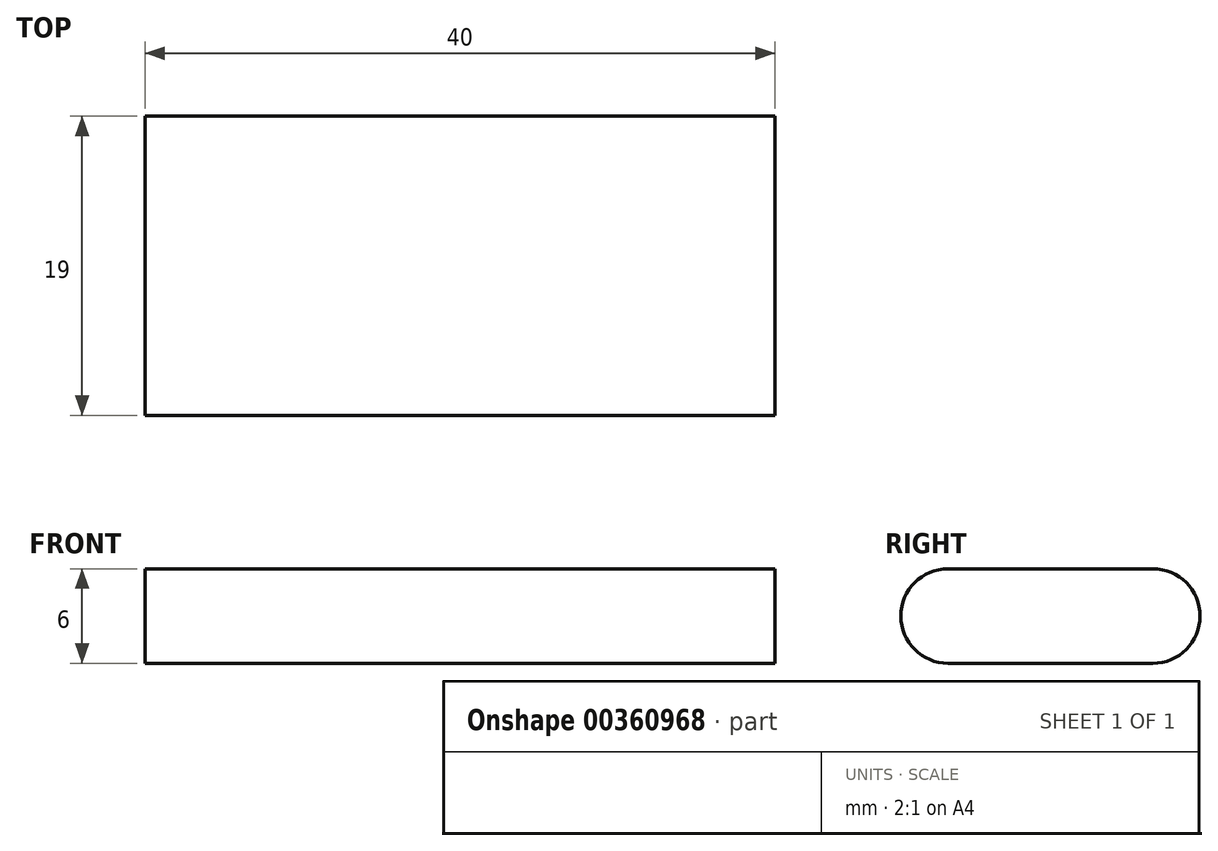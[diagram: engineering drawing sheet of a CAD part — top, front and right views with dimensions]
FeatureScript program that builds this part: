
annotation { "Feature Type Name" : "Feature", "Feature Type Description" : "" }
export const myFeature = defineFeature(function(context is Context, id is Id, definition is map)
    precondition{}
    {
        {
            var Q0;
            Q0=qCreatedBy(makeId("Right.planeOp"),FACE);
            var sketch = newSketch(context, id + "F0", { "sketchPlane" : qUnion([Q0])});
            skLineSegment(sketch, "E0.bottom", {"start": v(6.5, 3) * mm, "end": v(-6.5, 3) * mm});
            skLineSegment(sketch, "E0.top", {"start": v(6.5, -3) * mm, "end": v(-6.5, -3) * mm});
            skLineSegment(sketch, "E0.left", {"start": v(9.5, 0) * mm, "end": v(9.5, 0) * mm});
            skLineSegment(sketch, "E0.right", {"start": v(-9.5, 0) * mm, "end": v(-9.5, 0) * mm});
            skPoint(sketch, "E0.middle", {"position": v(0, 0) * mm});
            skPoint(sketch, "E1.visualSharp", {"position": v(-9.5, 3) * mm});
            skArc(sketch, "E1.filletArc", {"start": v(-6.5, 3) * mm, "mid": v(-8.62, 2.12) * mm, "end": v(-9.5, 0) * mm});
            skPoint(sketch, "E2.visualSharp", {"position": v(-9.5, -3) * mm});
            skArc(sketch, "E2.filletArc", {"start": v(-9.5, 0) * mm, "mid": v(-8.62, -2.12) * mm, "end": v(-6.5, -3) * mm});
            skPoint(sketch, "E3.visualSharp", {"position": v(9.5, 3) * mm});
            skArc(sketch, "E3.filletArc", {"start": v(9.5, 0) * mm, "mid": v(8.62, 2.12) * mm, "end": v(6.5, 3) * mm});
            skPoint(sketch, "E4.visualSharp", {"position": v(9.5, -3) * mm});
            skArc(sketch, "E4.filletArc", {"start": v(6.5, -3) * mm, "mid": v(8.62, -2.12) * mm, "end": v(9.5, 0) * mm});
            skSolve(sketch);
        }
        {
            var Q0;
            Q0=makeQuery(id+"F0.imprint","IMPRINT",FACE,{"disambiguationData":[TD([[makeQuery(id+"F0.imprint","IMPRINT",EDGE,{"derivedFrom":sQuery(id+"F0.wireOp",EDGE,"E0.bottom")}),1.0]])]});
            extrude(context, id + "F1", {"entities" : qUnion([Q0]), "endBound" : BoundingType.SYMMETRIC, "depth" : 40 * mm});
        }
    });
